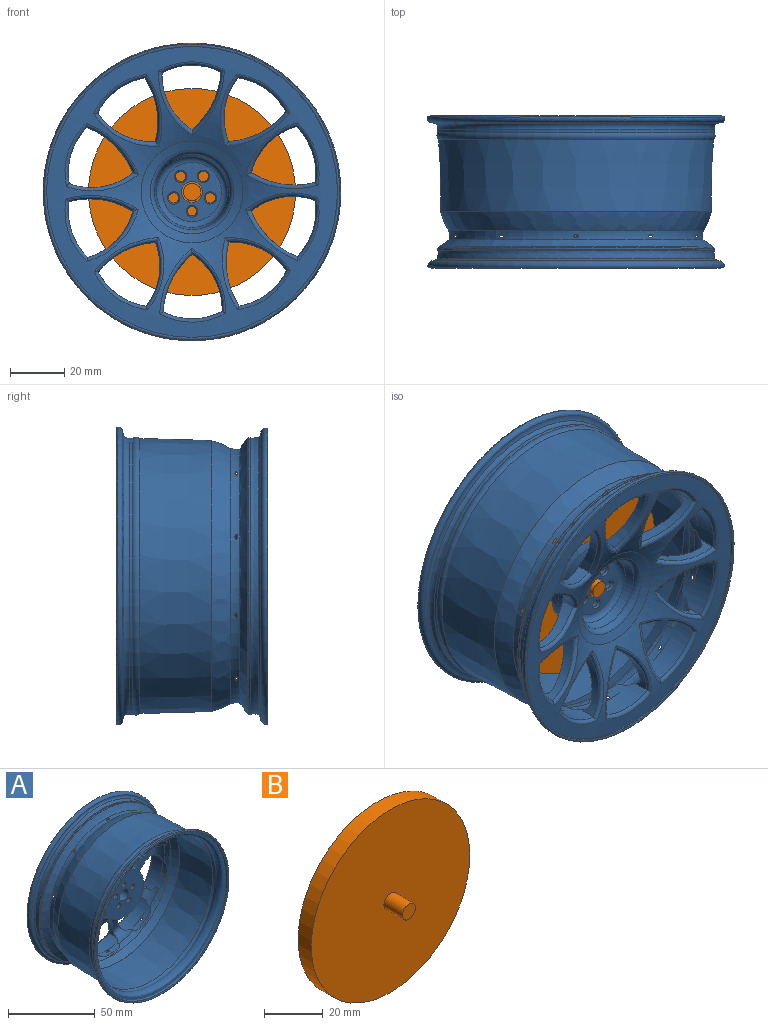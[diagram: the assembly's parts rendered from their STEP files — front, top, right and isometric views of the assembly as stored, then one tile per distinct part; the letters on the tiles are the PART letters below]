
ASSEMBLY  parts=2 mates=1
PART A: 113 faces, bbox 122.8x104.8x122.8 mm
  f0: revolved ~30.05x29.86mm, area 204.7mm2, adj f37,f39,f77,f79,f80,f81
  f1: revolved ~27.29x26.73mm, area 204.7mm2, adj f37,f39,f53,f54,f77,f78
  f2: revolved ~30.04x29.85mm, area 204.7mm2, adj f37,f39,f71,f73,f74,f75
  f3: revolved ~28.01x24.06mm, area 204.7mm2, adj f37,f39,f71,f72,f80,f82
  f4: revolved ~28.01x24.06mm, area 204.7mm2, adj f37,f39,f65,f67,f68,f69
  f5: revolved ~30.05x29.86mm, area 204.7mm2, adj f37,f39,f62,f64,f65,f66
  f6: revolved ~27.29x26.73mm, area 204.7mm2, adj f37,f39,f59,f61,f62,f63
  f7: revolved ~27.3x26.75mm, area 204.7mm2, adj f37,f39,f59,f60,f74,f76
  f8: revolved ~30.04x29.85mm, area 204.7mm2, adj f37,f39,f56,f57,f68,f70
  f9: plane 21.72x21.72mm, normal (0,1,0), area 243.6mm2, adj f10,f42,f48,f49,f50,f51,f52
  f10: torus R=10.79mm, axis (0,1,0), area 233.9mm2, adj f9,f11
  f11: cone r=13.96mm half-angle=14.6deg, axis (0,1,0), area 295.2mm2, adj f10,f12
  f12: torus R=16.31mm, axis (0,1,0), area 287.5mm2, adj f11,f13
  f13: cone r=18.74mm half-angle=67.1deg, axis (0,1,0), area 390.8mm2, adj f12,f14
  f14: torus R=49.61mm, axis (0,1,0), area 3377.9mm2, adj f13,f15,f83,f84,f85,f86,f87,f88
  f15: cylinder r=53.51mm len=107.01mm, axis (0,1,0), area 222.5mm2, adj f14,f16
  f16: torus R=53.98mm, axis (0,1,0), area 344.4mm2, adj f15,f17
  f17: torus R=52.67mm, axis (0,1,0), area 1046.9mm2, adj f16,f18
  f18: torus R=52.89mm, axis (0,1,0), area 732mm2, adj f17,f19
  f19: revolved ~102.25x102.25mm, area 980.4mm2, adj f18,f20
  f20: cylinder r=50.89mm len=101.77mm, axis (0,1,0), area 54.7mm2, adj f19,f21
  f21: plane 102.08x102.08mm, normal (0,1,0), area 49.3mm2, adj f20,f22
  f22: cylinder r=51.04mm len=102.08mm, axis (0,1,0), area 230.6mm2, adj f21,f23
  f23: cone r=50.72mm half-angle=39.5deg, axis (0,1,0), area 160.1mm2, adj f22,f24
  f24: revolved ~101.45x101.45mm, area 1491.9mm2, adj f23,f25
  f25: torus R=56.02mm, axis (0,1,0), area 986.5mm2, adj f24,f26,f53,f56,f59,f62,f65,f68
  f26: torus R=22.19mm, axis (0,1,0), area 2298.6mm2, adj f25,f27
  f27: cone r=50.64mm half-angle=1.6deg, axis (0,-1,0), area 8342.7mm2, adj f26,f28
  f28: torus R=49.05mm, axis (0,1,0), area 896.3mm2, adj f27,f29
  f29: cylinder r=50.87mm len=101.75mm, axis (0,1,0), area 400mm2, adj f28,f30
  f30: torus R=53.17mm, axis (0,1,0), area 701.7mm2, adj f29,f31
  f31: torus R=53.43mm, axis (0,1,0), area 652.1mm2, adj f30,f32
  f32: revolved ~109.57x109.57mm, area 937.1mm2, adj f31,f33
  f33: revolved ~109.47x109.47mm, area 535mm2, adj f32,f34
  f34: revolved ~107.43x107.43mm, area 3555.5mm2, adj f33,f35
  f35: cone r=49.18mm half-angle=1.6deg, axis (0,-1,0), area 8177.3mm2, adj f34,f36
  f36: revolved ~98.36x98.36mm, area 1627.3mm2, adj f35,f37
  f37: revolved ~94.11x94.11mm, area 721.5mm2, adj f0,f1,f2,f3,f4,f5,f6,f7
  f38: revolved ~27.3x26.75mm, area 204.7mm2, adj f37,f39,f53,f55,f56,f58
  f39: revolved ~45.97x45.97mm, area 1218.4mm2, adj f0,f1,f2,f3,f4,f5,f6,f7
  f40: cone r=15.93mm half-angle=12.3deg, axis (0,1,0), area 444.9mm2, adj f39,f41
  f41: plane 31.85x31.85mm, normal (0,-1,0), area 693.8mm2, adj f40,f42,f43,f44,f45,f46,f47
  f42: cylinder r=3.9mm len=7.81mm, axis (0,1,0), area 185.5mm2, adj f9,f41
  f43: cylinder r=1.75mm len=6.55mm, axis (0,1,0), area 71.9mm2, adj f41,f48
  f44: cylinder r=1.9mm len=6.55mm, axis (0,1,0), area 78.2mm2, adj f41,f50
  f45: cylinder r=1.9mm len=6.55mm, axis (0,1,0), area 78.2mm2, adj f41,f51
  f46: cylinder r=1.9mm len=6.55mm, axis (0,1,0), area 78.2mm2, adj f41,f52
  f47: cylinder r=1.9mm len=6.55mm, axis (0,1,0), area 78.2mm2, adj f41,f49
  f48: cone r=1.75mm half-angle=20deg, axis (0,1,0), area 13.1mm2, adj f9,f43
  f49: cone r=1.9mm half-angle=20deg, axis (0,1,0), area 14.2mm2, adj f9,f47
  f50: cone r=1.9mm half-angle=20deg, axis (0,1,0), area 14.2mm2, adj f9,f44
  f51: cone r=1.9mm half-angle=20deg, axis (0,1,0), area 14.2mm2, adj f9,f45
  f52: cone r=1.9mm half-angle=20deg, axis (0,1,0), area 14.2mm2, adj f9,f46
  f53: cylinder r=23.78mm len=21.68mm, axis (0,-1,0), area 255.2mm2, adj f1,f25,f37,f38,f54,f55,f110,f111
  f54: cylinder r=29.8mm len=21.27mm, axis (0,-1,0), area 98.7mm2, adj f1,f39,f53,f55,f110,f111
  f55: cylinder r=23.95mm len=21.05mm, axis (0,-1,0), area 100.5mm2, adj f38,f39,f53,f54,f111
  f56: cylinder r=23.78mm len=17.42mm, axis (0,-1,0), area 255.2mm2, adj f8,f25,f37,f38,f57,f58,f107,f108
  f57: cylinder r=23.95mm len=21.31mm, axis (0,-1,0), area 100.5mm2, adj f8,f39,f56,f58,f108
  f58: cylinder r=29.8mm len=23.46mm, axis (0,-1,0), area 98.7mm2, adj f38,f39,f56,f57,f107,f108
  f59: cylinder r=23.78mm len=21.68mm, axis (0,-1,0), area 255.2mm2, adj f6,f7,f25,f37,f60,f61,f104,f105
  f60: cylinder r=23.95mm len=21.05mm, axis (0,-1,0), area 100.5mm2, adj f7,f39,f59,f61,f105
  f61: cylinder r=29.8mm len=21.27mm, axis (0,-1,0), area 98.7mm2, adj f6,f39,f59,f60,f104,f105
  f62: cylinder r=23.78mm len=17.67mm, axis (0,-1,0), area 255.2mm2, adj f5,f6,f25,f37,f63,f64,f101,f102
  f63: cylinder r=23.95mm len=23.53mm, axis (0,-1,0), area 100.5mm2, adj f6,f39,f62,f64,f102
  f64: cylinder r=29.8mm len=21.1mm, axis (0,-1,0), area 98.7mm2, adj f5,f39,f62,f63,f101,f102
  f65: cylinder r=23.78mm len=20.56mm, axis (0,-1,0), area 255.2mm2, adj f4,f5,f25,f37,f66,f67,f98,f99
  f66: cylinder r=23.95mm len=17.01mm, axis (0,-1,0), area 100.5mm2, adj f5,f39,f65,f67,f99
  f67: cylinder r=29.8mm len=23.51mm, axis (0,-1,0), area 98.7mm2, adj f4,f39,f65,f66,f98,f99
  f68: cylinder r=23.78mm len=20.69mm, axis (0,-1,0), area 255.2mm2, adj f4,f8,f25,f37,f69,f70,f95,f96
  f69: cylinder r=23.95mm len=23.44mm, axis (0,-1,0), area 100.5mm2, adj f4,f39,f68,f70,f96
  f70: cylinder r=29.8mm len=16.94mm, axis (0,-1,0), area 98.7mm2, adj f8,f39,f68,f69,f95,f96
  f71: cylinder r=23.78mm len=20.69mm, axis (0,-1,0), area 255.2mm2, adj f2,f3,f25,f37,f72,f73,f92,f93
  f72: cylinder r=23.95mm len=23.44mm, axis (0,-1,0), area 100.5mm2, adj f3,f39,f71,f73,f93
  f73: cylinder r=29.8mm len=16.94mm, axis (0,-1,0), area 98.7mm2, adj f2,f39,f71,f72,f92,f93
  f74: cylinder r=23.78mm len=17.42mm, axis (0,-1,0), area 255.2mm2, adj f2,f7,f25,f37,f75,f76,f89,f90
  f75: cylinder r=23.95mm len=21.31mm, axis (0,-1,0), area 100.5mm2, adj f2,f39,f74,f76,f90
  f76: cylinder r=29.8mm len=23.46mm, axis (0,-1,0), area 98.7mm2, adj f7,f39,f74,f75,f89,f90
  f77: cylinder r=23.78mm len=17.67mm, axis (0,-1,0), area 255.2mm2, adj f0,f1,f25,f37,f78,f79,f86,f87
  f78: cylinder r=23.95mm len=23.53mm, axis (0,-1,0), area 100.5mm2, adj f1,f39,f77,f79,f87
  f79: cylinder r=29.8mm len=21.1mm, axis (0,-1,0), area 98.7mm2, adj f0,f39,f77,f78,f86,f87
  f80: cylinder r=23.78mm len=20.56mm, axis (0,-1,0), area 255.2mm2, adj f0,f3,f25,f37,f81,f82,f83,f84
  f81: cylinder r=23.95mm len=17.01mm, axis (0,-1,0), area 100.5mm2, adj f0,f39,f80,f82,f84
  f82: cylinder r=29.8mm len=23.51mm, axis (0,-1,0), area 98.7mm2, adj f3,f39,f80,f81,f83,f84
  f83: bspline ~29.97x7.83mm, area 55.5mm2, adj f14,f80,f82,f84,f85
  f84: bspline ~21.66x20.93mm, area 56.7mm2, adj f14,f80,f81,f82,f83,f85
  f85: bspline ~25.66x10.07mm, area 46.4mm2, adj f14,f80,f83,f84
  f86: bspline ~25.43x14.03mm, area 55.5mm2, adj f14,f77,f79,f87,f88
  f87: bspline ~29.67x8.13mm, area 56.7mm2, adj f14,f77,f78,f79,f86,f88
  f88: bspline ~22.03x16.2mm, area 46.4mm2, adj f14,f77,f86,f87
  f89: bspline ~28.82x7.81mm, area 55.5mm2, adj f14,f74,f76,f90,f91
  f90: bspline ~26.58x13.94mm, area 56.7mm2, adj f14,f74,f75,f76,f89,f91
  f91: bspline ~21.85x16.45mm, area 46.4mm2, adj f14,f74,f89,f90
  f92: bspline ~21.63x20.88mm, area 55.5mm2, adj f14,f71,f73,f93,f94
  f93: bspline ~29.61x8.76mm, area 56.7mm2, adj f14,f71,f72,f73,f92,f94
  f94: bspline ~25.76x9.85mm, area 46.4mm2, adj f14,f71,f92,f93
  f95: bspline ~21.63x20.88mm, area 55.5mm2, adj f14,f68,f70,f96,f97
  f96: bspline ~29.61x8.76mm, area 56.7mm2, adj f14,f68,f69,f70,f95,f97
  f97: bspline ~25.76x9.85mm, area 46.4mm2, adj f14,f68,f95,f96
  f98: bspline ~29.97x7.83mm, area 55.5mm2, adj f14,f65,f67,f99,f100
  f99: bspline ~21.66x20.93mm, area 56.7mm2, adj f14,f65,f66,f67,f98,f100
  f100: bspline ~25.66x10.07mm, area 46.4mm2, adj f14,f65,f98,f99
  f101: bspline ~25.43x14.03mm, area 55.5mm2, adj f14,f62,f64,f102,f103
  f102: bspline ~29.67x8.13mm, area 56.7mm2, adj f14,f62,f63,f64,f101,f103
  f103: bspline ~22.03x16.2mm, area 46.4mm2, adj f14,f62,f101,f102
  f104: bspline ~27.42x13.79mm, area 55.5mm2, adj f14,f59,f61,f105,f106
  f105: bspline ~26.66x14.92mm, area 56.7mm2, adj f14,f59,f60,f61,f104,f106
  f106: bspline ~27.03x5.09mm, area 46.4mm2, adj f14,f59,f104,f105
  f107: bspline ~28.82x7.81mm, area 55.5mm2, adj f14,f56,f58,f108,f109
  f108: bspline ~26.58x13.94mm, area 56.7mm2, adj f14,f56,f57,f58,f107,f109
  f109: bspline ~21.85x16.45mm, area 46.4mm2, adj f14,f56,f107,f108
  f110: bspline ~27.42x13.79mm, area 55.5mm2, adj f14,f53,f54,f111,f112
  f111: bspline ~26.66x14.92mm, area 56.7mm2, adj f14,f53,f54,f55,f110,f112
  f112: bspline ~27.03x5.09mm, area 46.4mm2, adj f14,f53,f110,f111
PART B: 5 faces, bbox 76.2x15.2x76.2 mm
  f0: cylinder r=38.1mm len=76.2mm, axis (0,1,0), area 1520.1mm2, adj f1,f2
  f1: plane 76.2x76.2mm, normal (0,-1,0), area 4528.7mm2, adj f0,f3
  f2: plane 76.2x76.2mm, normal (0,1,0), area 4560.4mm2, adj f0
  f3: cylinder r=3.17mm len=8.89mm, axis (0,1,0), area 177.3mm2, adj f1,f4
  f4: plane 6.35x6.35mm, normal (0,-1,0), area 31.7mm2, adj f3
PLACE A rot(axis=(1,0,0),180deg) t=(65.84,6.5,-50.07)mm
PLACE B t=(65.84,12.91,-50.07)mm
MATE revolute A.f10 <-> B.f0  axis (0,-1,0) through (65.84,-1.06,-50.07)mm
